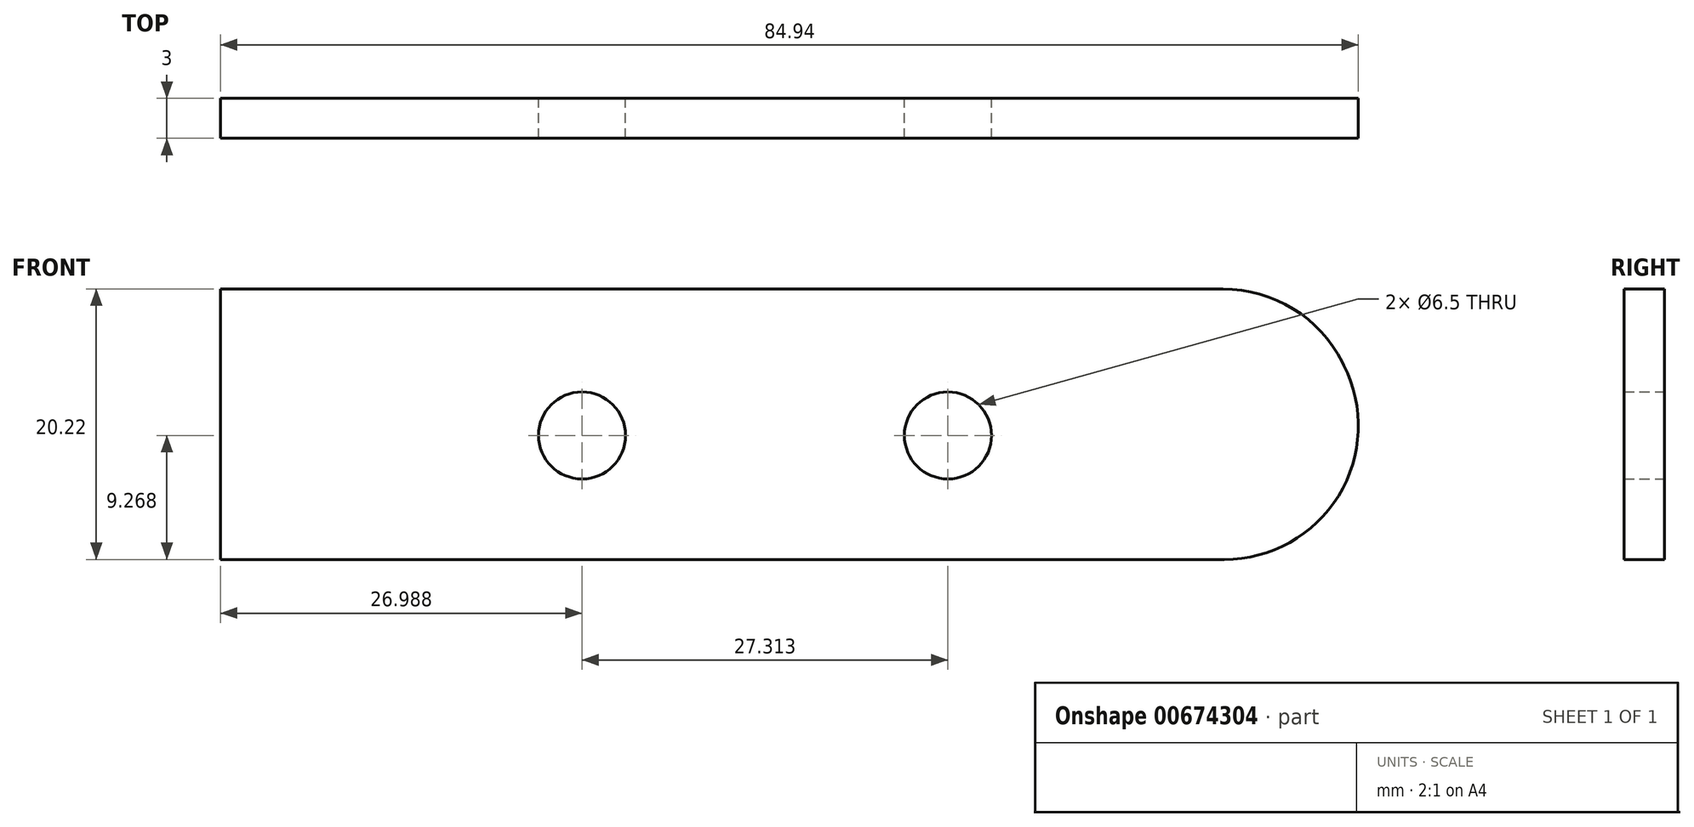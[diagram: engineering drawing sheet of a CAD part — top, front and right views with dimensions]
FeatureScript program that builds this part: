
annotation { "Feature Type Name" : "Feature", "Feature Type Description" : "" }
export const myFeature = defineFeature(function(context is Context, id is Id, definition is map)
    precondition{}
    {
        {
            var Q0;
            Q0=qCreatedBy(makeId("Front.planeOp"),FACE);
            var sketch = newSketch(context, id + "F0", { "sketchPlane" : qUnion([Q0])});
            skLineSegment(sketch, "E0.bottom", {"start": v(-22.37, 6.18) * mm, "end": v(52.45, 6.18) * mm});
            skLineSegment(sketch, "E0.top", {"start": v(-22.37, -14.04) * mm, "end": v(52.57, -14.04) * mm});
            skLineSegment(sketch, "E0.right", {"start": v(61.38, 0.7) * mm, "end": v(61.5, 0.47) * mm});
            skPoint(sketch, "E1.visualSharp", {"position": v(58.6, 6.18) * mm});
            skArc(sketch, "E1.filletArc", {"start": v(61.38, 0.7) * mm, "mid": v(57.7, 4.7) * mm, "end": v(52.45, 6.18) * mm});
            skPoint(sketch, "E2.visualSharp", {"position": v(68.83, -14.04) * mm});
            skArc(sketch, "E2.filletArc", {"start": v(52.57, -14.04) * mm, "mid": v(61.08, -9.28) * mm, "end": v(61.5, 0.47) * mm});
            skLineSegment(sketch, "E3", {"start": v(-22.37, -14.04) * mm, "end": v(-22.37, 6.18) * mm});
            skPoint(sketch, "E0.left.start.orphan", {"position": v(-31.4, 6.18) * mm});
            skSolve(sketch);
        }
        {
            var Q0;
            Q0=qSketchRegion(id+"F0",true);
            extrude(context, id + "F1", {"entities" : qUnion([Q0]), "depth" : 3 * mm, "offsetDistance" : 25 * mm});
        }
        {
            var Q0;
            Q0=makeQuery(id+"F1.opExtrude","CAP_FACE",FACE,{"disambiguationData":[OSD([sQuery(id+"F0.wireOp",EDGE,"E0.bottom"),sQuery(id+"F0.wireOp",EDGE,"E0.top"),sQuery(id+"F0.wireOp",EDGE,"E0.right"),sQuery(id+"F0.wireOp",EDGE,"E1.filletArc"),sQuery(id+"F0.wireOp",EDGE,"E2.filletArc"),sQuery(id+"F0.wireOp",EDGE,"E3")])],"isStart":true});
            var sketch = newSketch(context, id + "F2", { "sketchPlane" : qUnion([Q0])});
            skPoint(sketch, "E4", {"position": v(-31.93, -4.77) * mm});
            skPoint(sketch, "E5", {"position": v(-4.62, -4.77) * mm});
            skSolve(sketch);
        }
        {
            var Q0;
            Q0=sQuery(id+"F2.wireOp",VERTEX,"E4");
            var Q1;
            Q1=sQuery(id+"F2.wireOp",VERTEX,"E5");
            var Q2;
            Q2=makeQuery(id+"F1.opExtrude","SWEPT_BODY",BODY,{"disambiguationData":[OSD([sQuery(id+"F0.wireOp",EDGE,"E0.bottom"),sQuery(id+"F0.wireOp",EDGE,"E0.top"),sQuery(id+"F0.wireOp",EDGE,"E0.right"),sQuery(id+"F0.wireOp",EDGE,"E1.filletArc"),sQuery(id+"F0.wireOp",EDGE,"E2.filletArc"),sQuery(id+"F0.wireOp",EDGE,"E3")])]});
            hole(context, id + "F3", {"style" : HoleStyle.C_BORE, "endStyle" : HoleEndStyle.BLIND, "standardTappedOrClearance" : lookupTablePath({ "standard" : "ISO", "fit" : "Normal", "size" : "M3", "type" : "Clearance" }), "standardBlindInLast" : lookupTablePath({ "fit" : "Standard", "standard" : "ISO", "size" : "M3", "type" : "Clearance" }), "holeDiameter" : 3.3 * mm, "cBoreDiameter" : 6.5 * mm, "cBoreDepth" : 3 * mm, "majorDiameter" : 5 * mm, "holeDepth" : 14.4 * mm, "isTappedThrough" : true, "tappedDepth" : 12 * mm, "tapClearance" : 3, "startFromSketch" : true, "locations" : qUnion([Q0, Q1]), "scope" : qUnion([Q2])});
        }
    });
